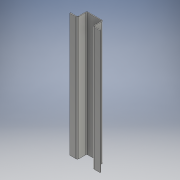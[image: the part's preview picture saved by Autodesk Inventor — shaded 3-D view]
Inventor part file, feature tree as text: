
AUTODESK INVENTOR PART (.ipt)
format: ipt  version: 2017 (Build 210142000, 142)  size: 158,720 bytes
history: native  units: mm
features: sheet_metal_op x3, other x2, sketch x1
ambient origin geometry x8: Origin, YZ Plane, XZ Plane, XY Plane, X Axis, Y Axis, Z Axis, Center Point
bodies: Solid1 (feature_tree)
feature tree (6):
  sheet_metal_op  "Contour Flange1"
  sketch  "Sketch1"  dims[d0=30.0mm d1=15.0mm d3=18.5mm d4=15.0mm d5=15.0mm d6=1.5mm d7=0.75mm d8=3.0mm d9=1.5mm d10=245.0mm d11=1.5mm d12=0.5mm d13=6.0mm d14=1.5mm d15=1.5mm]
  other  "Plate1"
  sheet_metal_op  "Bend1"
  sheet_metal_op  "Corner1"
  other  "Definition1"
